# Revit family: LEO_D_S
name_source: partatom
category: Mechanical Equipment
revit_build: Autodesk Revit LT 2018 (Build: 20180329_1100(x64)
units: mm (PartAtom-declared; Revit-internal decimal feet)

## family parameters
Cut with Voids When Loaded = No
Host = Face
Part Type = Normal
Room Calculation Point = No
Round Connector Dimension = Use Diameter
Shared = No

## types (9) — shared parameters
Description = Destratifikátor
Distance from the ceiling = 1000 mm  [stored 3.28084 ft]
Fan = axial, single-phase, AC with 3-speed motor
IP = 54
Load classification = Silnik
Manufacturer = Hydronic Systems Prague s.r.o.
Mass of unit = 8.90 kg
Material = EPP-grey
Power factor = 1
Supply voltage = 230 V
Type Comments = vnitřní instalace, podstropní, vertikální; max. teplota okolí +50°C; IP54; Qmax=2500 m3/h při 3. rychlosti
URL = www.hydronic.cz
zero-valued in all types: Default Elevation

## per-type parameters (varying)
| type | Airflow | Apparent power | Assembly Code | Max. current consumption | Model | Standard equipment |
| LEO DT S, 1 rychlost | 1900.0 m³/h | 69 VA | 52074; LEO DT S (vč. integrovaného pokojového termostatu)  - 1 rychlost | 0 A | LEO DT S | pokojový termostat umístěný na opláštění jednotky |
| LEO DT S, 2 rychlost | 2200.0 m³/h | 92 VA | 52074; LEO DT S (vč. integrovaného pokojového termostatu)  - 2 rychlost | 0 A | LEO DT S | pokojový termostat umístěný na opláštění jednotky |
| LEO DT S, 3 rychlost | 2500.0 m³/h | 115 VA | 52074; LEO DT S (vč. integrovaného pokojového termostatu)  - 3 rychlost | 1 A | LEO DT S | pokojový termostat umístěný na opláštění jednotky |
| LEO D S BMS, 1 rychlost | 1900.0 m³/h | 69 VA | 52080; LEO D S BMS (vč. DRV-D + 1xPT1000)  - 1 rychlost | 0 A | LEO D S BMS | DRV D + PT-1000 |
| LEO D S BMS, 2 rychlost | 2200.0 m³/h | 92 VA | 52080; LEO D S BMS (vč. DRV-D + 1xPT1000)  - 2 rychlost | 0 A | LEO D S BMS | DRV D + PT-1000 |
| LEO D S BMS, 3 rychlost | 2500.0 m³/h | 115 VA | 52080; LEO D S BMS (vč. DRV-D + 1xPT1000)  - 3 rychlost | 1 A | LEO D S BMS | DRV D + PT-1000 |
| LEO D S, 1 rychlost | 1900.0 m³/h | 69 VA | 52070; LEO D S  - 1 rychlost | 0 A | LEO D S |  |
| LEO D S, 2 rychlost | 2200.0 m³/h | 92 VA | 52070; LEO D S  - 2 rychlost | 0 A | LEO D S |  |
| LEO D S, 3 rychlost | 2500.0 m³/h | 115 VA | 52070; LEO D S  - 3 rychlost | 1 A | LEO D S |  |

note: [stored X ft] marks values corroborated as IEEE doubles in the binary element streams (Revit-internal decimal feet)
